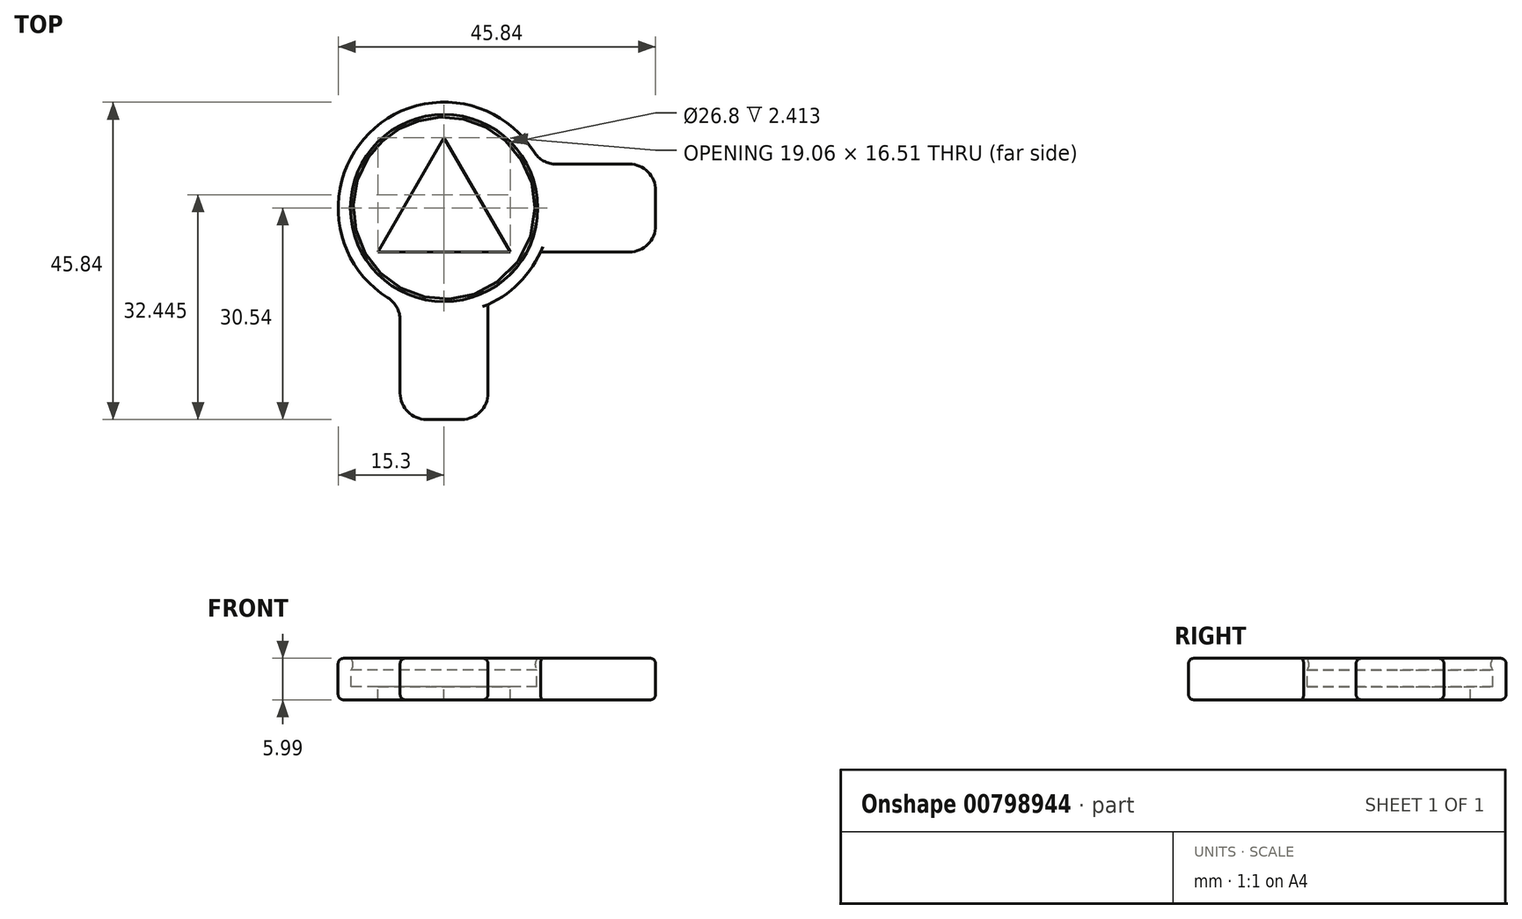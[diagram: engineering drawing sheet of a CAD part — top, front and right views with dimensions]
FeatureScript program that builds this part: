
annotation { "Feature Type Name" : "Feature", "Feature Type Description" : "" }
export const myFeature = defineFeature(function(context is Context, id is Id, definition is map)
    precondition{}
    {
        {
            var Q0;
            Q0=qCreatedBy(makeId("Front.planeOp"),FACE);
            var sketch = newSketch(context, id + "F0", { "sketchPlane" : qUnion([Q0])});
            skLineSegment(sketch, "E0", {"start": v(15.3, 4.17) * mm, "end": v(15.3, 0) * mm});
            skLineSegment(sketch, "E1", {"start": v(15.3, 0) * mm, "end": v(0, 0) * mm});
            skArc(sketch, "E2", {"start": v(15.3, 4.17) * mm, "mid": v(13.5, 4.2) * mm, "end": v(13.53, 5.99) * mm});
            skLineSegment(sketch, "E3", {"start": v(0, 10.9) * mm, "end": v(0, -2.45) * mm, "construction": true});
            skLineSegment(sketch, "E4", {"start": v(0, 0) * mm, "end": v(0, 1.9) * mm});
            skLineSegment(sketch, "E5", {"start": v(0, 1.9) * mm, "end": v(13.4, 1.9) * mm});
            skLineSegment(sketch, "E6", {"start": v(13.4, 1.9) * mm, "end": v(13.4, 4.32) * mm});
            skLineSegment(sketch, "E7", {"start": v(15.3, 4.17) * mm, "end": v(15.3, 5.99) * mm});
            skLineSegment(sketch, "E8", {"start": v(15.3, 5.99) * mm, "end": v(13.53, 5.99) * mm});
            skSolve(sketch);
        }
        {
            var Q0;
            Q0=qSketchRegion(id+"F0",true);
            var Q1;
            Q1=sQuery(id+"F0.wireOp",EDGE,"E3");
            revolve(context, id + "F1", {"surfaceOperationType" : NewSurfaceOperationType.NEW, "entities" : qUnion([Q0]), "axis" : qUnion([Q1]), "revolveType" : RevolveType.FULL});
        }
        {
            var Q0;
            Q0=makeQuery(id+"F1.opRevolve","SWEPT_FACE",FACE,{"disambiguationData":[OSD([sQuery(id+"F0.wireOp",EDGE,"E8")])]});
            var sketch = newSketch(context, id + "F2", { "sketchPlane" : qUnion([Q0])});
            skLineSegment(sketch, "E9.bottom", {"start": v(30.54, 6.35) * mm, "end": v(13.92, 6.35) * mm});
            skLineSegment(sketch, "E9.top", {"start": v(30.54, -6.35) * mm, "end": v(13.92, -6.35) * mm});
            skLineSegment(sketch, "E9.left", {"start": v(30.54, 6.35) * mm, "end": v(30.54, -6.35) * mm});
            skLineSegment(sketch, "E10.bottom", {"start": v(6.35, -30.54) * mm, "end": v(-6.35, -30.54) * mm});
            skLineSegment(sketch, "E10.left", {"start": v(6.35, -30.54) * mm, "end": v(6.35, -13.92) * mm});
            skLineSegment(sketch, "E10.right", {"start": v(-6.35, -30.54) * mm, "end": v(-6.35, -13.92) * mm});
            skArc(sketch, "E11.0", {"start": v(-6.35, -13.92) * mm, "mid": v(0, -15.3) * mm, "end": v(6.35, -13.92) * mm});
            skArc(sketch, "E12.trimOffspring", {"start": v(13.92, -6.35) * mm, "mid": v(15.3, 0) * mm, "end": v(13.92, 6.35) * mm});
            skSolve(sketch);
        }
        {
            var Q0;
            Q0=qSketchRegion(id+"F2",true);
            var Q1;
            Q1=makeQuery(id+"F1.opRevolve","SWEPT_FACE",FACE,{"disambiguationData":[OSD([sQuery(id+"F0.wireOp",EDGE,"E1")])]});
            extrude(context, id + "F3", {"entities" : qUnion([Q0]), "operationType" : NewBodyOperationType.ADD, "endBound" : BoundingType.UP_TO_SURFACE, "oppositeDirection" : true, "depth" : 25.4 * mm, "endBoundEntityFace" : qUnion([Q1]), "offsetDistance" : 25.4 * mm});
        }
        {
            var Q0;
            Q0=makeQuery(id+"F3.opExtrude","SWEPT_EDGE",EDGE,{"disambiguationData":[OSD([sQuery(id+"F2.wireOp",EDGE,"E10.bottom"),sQuery(id+"F2.wireOp",EDGE,"E10.right")])]});
            var Q1;
            Q1=makeQuery(id+"F3.opExtrude","SWEPT_EDGE",EDGE,{"disambiguationData":[OSD([sQuery(id+"F0.wireOp",EDGE,"E7"),sQuery(id+"F0.wireOp",EDGE,"E8"),sQuery(id+"F2.wireOp",EDGE,"E10.right"),sQuery(id+"F2.wireOp",EDGE,"E11.0")])]});
            var Q2;
            Q2=makeQuery(id+"F3.opExtrude","SWEPT_EDGE",EDGE,{"disambiguationData":[OSD([sQuery(id+"F2.wireOp",EDGE,"E10.bottom"),sQuery(id+"F2.wireOp",EDGE,"E10.left")])]});
            var Q3;
            Q3=makeQuery(id+"F3.opExtrude","SWEPT_EDGE",EDGE,{"disambiguationData":[OSD([sQuery(id+"F0.wireOp",EDGE,"E7"),sQuery(id+"F0.wireOp",EDGE,"E8"),sQuery(id+"F2.wireOp",EDGE,"E10.left"),sQuery(id+"F2.wireOp",EDGE,"E11.0")])]});
            var Q4;
            Q4=makeQuery(id+"F3.opExtrude","SWEPT_EDGE",EDGE,{"disambiguationData":[OSD([sQuery(id+"F0.wireOp",EDGE,"E7"),sQuery(id+"F0.wireOp",EDGE,"E8"),sQuery(id+"F2.wireOp",EDGE,"E9.top"),sQuery(id+"F2.wireOp",EDGE,"E12.trimOffspring")])]});
            var Q5;
            Q5=makeQuery(id+"F3.opExtrude","SWEPT_EDGE",EDGE,{"disambiguationData":[OSD([sQuery(id+"F2.wireOp",EDGE,"E9.top"),sQuery(id+"F2.wireOp",EDGE,"E9.left")])]});
            var Q6;
            Q6=makeQuery(id+"F3.opExtrude","SWEPT_EDGE",EDGE,{"disambiguationData":[OSD([sQuery(id+"F2.wireOp",EDGE,"E9.bottom"),sQuery(id+"F2.wireOp",EDGE,"E9.left")])]});
            var Q7;
            Q7=makeQuery(id+"F3.opExtrude","SWEPT_EDGE",EDGE,{"disambiguationData":[OSD([sQuery(id+"F0.wireOp",EDGE,"E7"),sQuery(id+"F0.wireOp",EDGE,"E8"),sQuery(id+"F2.wireOp",EDGE,"E9.bottom"),sQuery(id+"F2.wireOp",EDGE,"E12.trimOffspring")])]});
            fillet(context, id + "F4", {"entities" : qUnion([Q0, Q1, Q2, Q3, Q4, Q5, Q6, Q7]), "radius" : 3.8 * mm, "tangentPropagation" : true, "allowEdgeOverflow" : false});
        }
        {
            var Q0;
            Q0=makeQuery(id+"F3.opExtrude","CAP_EDGE",EDGE,{"disambiguationData":[OSD([sQuery(id+"F2.wireOp",EDGE,"E10.bottom")])],"isStart":true});
            var Q1;
            Q1=makeQuery(id+"F3.opExtrude","CAP_EDGE",EDGE,{"disambiguationData":[OSD([sQuery(id+"F2.wireOp",EDGE,"E10.bottom")])],"isStart":false});
            fillet(context, id + "F5", {"entities" : qUnion([Q0, Q1]), "radius" : 0.76 * mm, "tangentPropagation" : true, "allowEdgeOverflow" : false});
        }
        {
            var Q0;
            Q0=makeQuery(id+"F1.opRevolve","SWEPT_FACE",FACE,{"disambiguationData":[OSD([sQuery(id+"F0.wireOp",EDGE,"E5")])]});
            var sketch = newSketch(context, id + "F6", { "sketchPlane" : qUnion([Q0])});
            skLineSegment(sketch, "E13", {"start": v(-9.53, -6.35) * mm, "end": v(0, 10.16) * mm});
            skLineSegment(sketch, "E14", {"start": v(0, 10.16) * mm, "end": v(9.53, -6.35) * mm});
            skLineSegment(sketch, "E15", {"start": v(9.53, -6.35) * mm, "end": v(-9.53, -6.35) * mm});
            skSolve(sketch);
        }
        {
            var Q0;
            Q0 = qSketchRegion(id + "F6", true);
            extrude(context, id + "F7", {"entities" : qUnion([Q0]), "operationType" : NewBodyOperationType.REMOVE, "oppositeDirection" : true, "depth" : 25.4 * mm, "offsetDistance" : 25.4 * mm});
        }
    });
